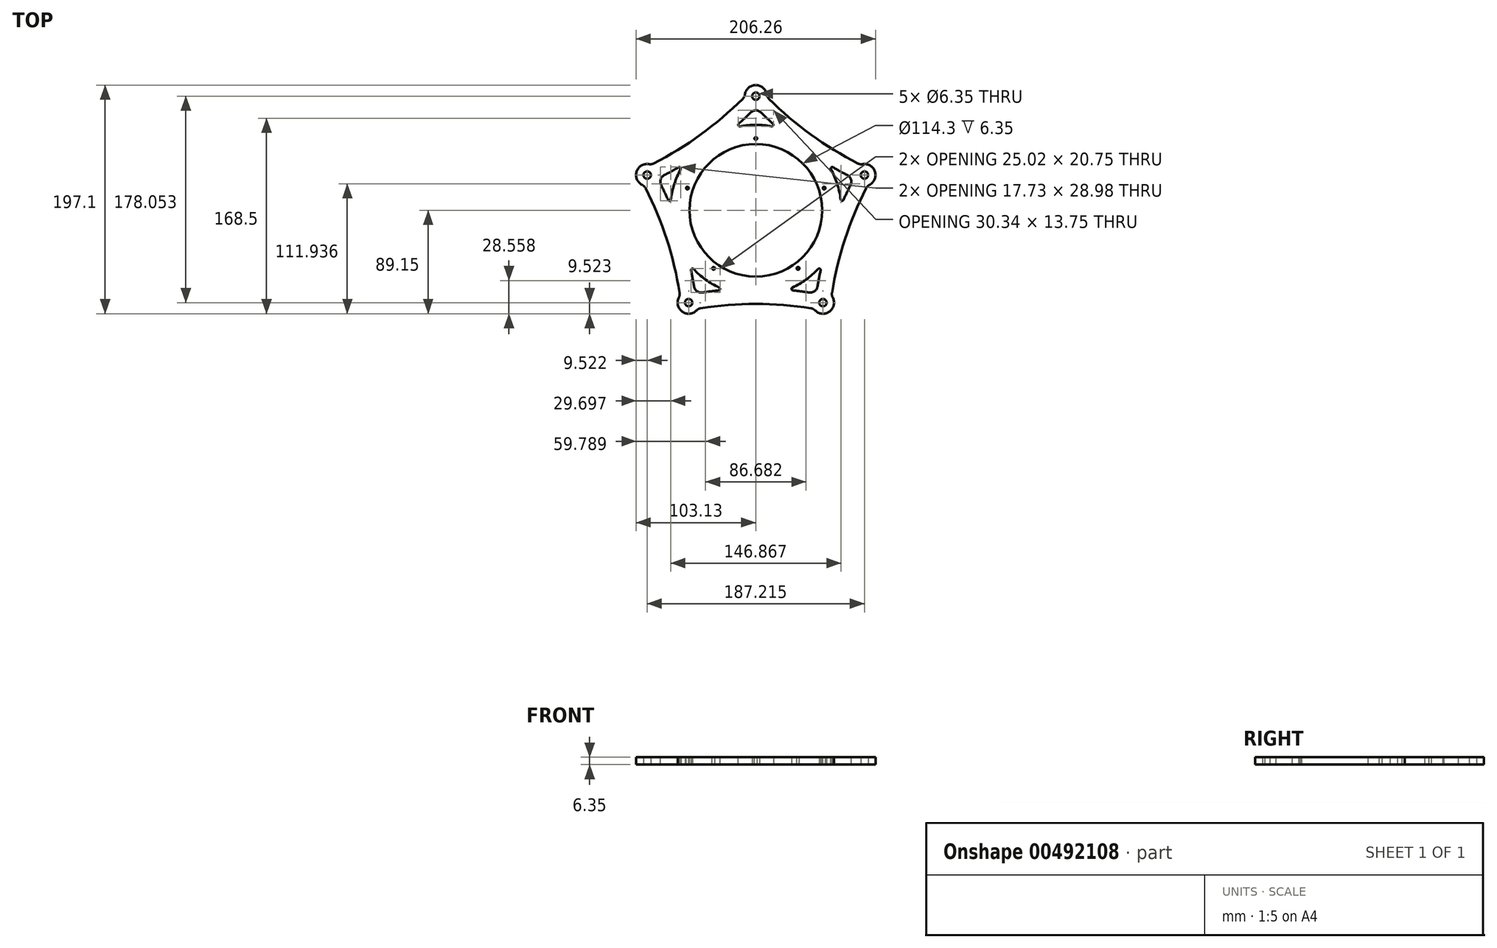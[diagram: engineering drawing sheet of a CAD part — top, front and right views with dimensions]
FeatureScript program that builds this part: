
annotation { "Feature Type Name" : "Feature", "Feature Type Description" : "" }
export const myFeature = defineFeature(function(context is Context, id is Id, definition is map)
    precondition{}
    {
        {
            var Q0;
            Q0=qCreatedBy(makeId("Top.planeOp"),FACE);
            var sketch = newSketch(context, id + "F0", { "sketchPlane" : qUnion([Q0])});
            skCircle(sketch, "E0", {"center": v(0, 0) * mm, "radius": 98.43 * mm, "construction": true});
            skCircle(sketch, "E1", {"center": v(0, 98.43) * mm, "radius": 3.18 * mm});
            skCircle(sketch, "E2.1.0", {"center": v(-93.6, 30.41) * mm, "radius": 3.18 * mm});
            skCircle(sketch, "E2.2.0", {"center": v(-57.85, -79.63) * mm, "radius": 3.18 * mm});
            skCircle(sketch, "E2.3.0", {"center": v(57.85, -79.63) * mm, "radius": 3.18 * mm});
            skCircle(sketch, "E2.4.0", {"center": v(93.6, 30.41) * mm, "radius": 3.18 * mm});
            skCircle(sketch, "E3", {"center": v(0, 98.43) * mm, "radius": 9.53 * mm, "construction": true});
            skCircle(sketch, "E4.1.0", {"center": v(-93.6, 30.41) * mm, "radius": 9.53 * mm, "construction": true});
            skCircle(sketch, "E4.2.0", {"center": v(-57.85, -79.63) * mm, "radius": 9.53 * mm, "construction": true});
            skCircle(sketch, "E4.3.0", {"center": v(57.85, -79.63) * mm, "radius": 9.53 * mm, "construction": true});
            skCircle(sketch, "E4.4.0", {"center": v(93.6, 30.41) * mm, "radius": 9.53 * mm, "construction": true});
            skArc(sketch, "E5", {"start": v(-90.23, 39.32) * mm, "mid": v(-47.46, 65.32) * mm, "end": v(-9.51, 97.96) * mm});
            skArc(sketch, "E6", {"start": v(9.51, 97.96) * mm, "mid": v(47.46, 65.32) * mm, "end": v(90.23, 39.32) * mm});
            skArc(sketch, "E7", {"start": v(96.1, 21.22) * mm, "mid": v(76.79, -24.95) * mm, "end": v(65.28, -73.66) * mm});
            skArc(sketch, "E8", {"start": v(49.89, -84.85) * mm, "mid": v(0, -80.74) * mm, "end": v(-49.89, -84.85) * mm});
            skArc(sketch, "E9", {"start": v(-65.28, -73.66) * mm, "mid": v(-76.79, -24.95) * mm, "end": v(-96.1, 21.22) * mm});
            skLineSegment(sketch, "E10", {"start": v(0, 0) * mm, "end": v(-93.6, 30.41) * mm, "construction": true});
            skLineSegment(sketch, "E11", {"start": v(0, 0) * mm, "end": v(93.6, 30.41) * mm, "construction": true});
            skLineSegment(sketch, "E12", {"start": v(0, 0) * mm, "end": v(57.85, -79.63) * mm, "construction": true});
            skLineSegment(sketch, "E13", {"start": v(0, 0) * mm, "end": v(-57.85, -79.63) * mm, "construction": true});
            skLineSegment(sketch, "E14", {"start": v(0, 0) * mm, "end": v(0, 98.43) * mm, "construction": true});
            skArc(sketch, "E15", {"start": v(-84.55, 27.47) * mm, "mid": v(-39.62, 54.54) * mm, "end": v(0, 88.9) * mm});
            skArc(sketch, "E16", {"start": v(0, 88.9) * mm, "mid": v(39.62, 54.54) * mm, "end": v(84.55, 27.47) * mm});
            skArc(sketch, "E17", {"start": v(84.55, 27.47) * mm, "mid": v(64.1, -20.83) * mm, "end": v(52.25, -71.92) * mm});
            skArc(sketch, "E18", {"start": v(52.25, -71.92) * mm, "mid": v(0, -67.4) * mm, "end": v(-52.25, -71.92) * mm});
            skArc(sketch, "E19", {"start": v(-52.25, -71.92) * mm, "mid": v(-64.1, -20.83) * mm, "end": v(-84.55, 27.47) * mm});
            skArc(sketch, "E20", {"start": v(-96.1, 21.22) * mm, "mid": v(-102.67, 33.36) * mm, "end": v(-90.23, 39.32) * mm});
            skArc(sketch, "E21", {"start": v(-9.51, 97.96) * mm, "mid": v(0, 107.95) * mm, "end": v(9.51, 97.96) * mm});
            skArc(sketch, "E22", {"start": v(90.23, 39.32) * mm, "mid": v(102.67, 33.36) * mm, "end": v(96.1, 21.22) * mm});
            skArc(sketch, "E23", {"start": v(65.28, -73.66) * mm, "mid": v(63.45, -87.33) * mm, "end": v(49.89, -84.85) * mm});
            skArc(sketch, "E24", {"start": v(-65.28, -73.66) * mm, "mid": v(-63.45, -87.33) * mm, "end": v(-49.89, -84.85) * mm});
            skSolve(sketch);
        }
        {
            var Q0;
            Q0 = qSketchRegion(id + "F0", true);
            extrude(context, id + "F1", {"entities" : qUnion([Q0]), "depth" : 6.35 * mm});
        }
        {
            var Q0;
            Q0=makeQuery(id+"F1.opExtrude","SWEPT_EDGE",EDGE,{"disambiguationData":[OSD([sQuery(id+"F0.wireOp",EDGE,"E15"),sQuery(id+"F0.wireOp",EDGE,"E16")])]});
            var Q1;
            Q1=makeQuery(id+"F1.opExtrude","SWEPT_EDGE",EDGE,{"disambiguationData":[OSD([sQuery(id+"F0.wireOp",EDGE,"E5"),sQuery(id+"F0.wireOp",EDGE,"E21")])]});
            var Q2;
            Q2=makeQuery(id+"F1.opExtrude","SWEPT_EDGE",EDGE,{"disambiguationData":[OSD([sQuery(id+"F0.wireOp",EDGE,"E6"),sQuery(id+"F0.wireOp",EDGE,"E21")])]});
            var Q3;
            Q3=makeQuery(id+"F1.opExtrude","SWEPT_EDGE",EDGE,{"disambiguationData":[OSD([sQuery(id+"F0.wireOp",EDGE,"E16"),sQuery(id+"F0.wireOp",EDGE,"E17")])]});
            var Q4;
            Q4=makeQuery(id+"F1.opExtrude","SWEPT_EDGE",EDGE,{"disambiguationData":[OSD([sQuery(id+"F0.wireOp",EDGE,"E7"),sQuery(id+"F0.wireOp",EDGE,"E22")])]});
            var Q5;
            Q5=makeQuery(id+"F1.opExtrude","SWEPT_EDGE",EDGE,{"disambiguationData":[OSD([sQuery(id+"F0.wireOp",EDGE,"E6"),sQuery(id+"F0.wireOp",EDGE,"E22")])]});
            var Q6;
            Q6=makeQuery(id+"F1.opExtrude","SWEPT_EDGE",EDGE,{"disambiguationData":[OSD([sQuery(id+"F0.wireOp",EDGE,"E7"),sQuery(id+"F0.wireOp",EDGE,"E23")])]});
            var Q7;
            Q7=makeQuery(id+"F1.opExtrude","SWEPT_EDGE",EDGE,{"disambiguationData":[OSD([sQuery(id+"F0.wireOp",EDGE,"E8"),sQuery(id+"F0.wireOp",EDGE,"E23")])]});
            var Q8;
            Q8=makeQuery(id+"F1.opExtrude","SWEPT_EDGE",EDGE,{"disambiguationData":[OSD([sQuery(id+"F0.wireOp",EDGE,"E17"),sQuery(id+"F0.wireOp",EDGE,"E18")])]});
            var Q9;
            Q9=makeQuery(id+"F1.opExtrude","SWEPT_EDGE",EDGE,{"disambiguationData":[OSD([sQuery(id+"F0.wireOp",EDGE,"E8"),sQuery(id+"F0.wireOp",EDGE,"E24")])]});
            var Q10;
            Q10=makeQuery(id+"F1.opExtrude","SWEPT_EDGE",EDGE,{"disambiguationData":[OSD([sQuery(id+"F0.wireOp",EDGE,"E9"),sQuery(id+"F0.wireOp",EDGE,"E24")])]});
            var Q11;
            Q11=makeQuery(id+"F1.opExtrude","SWEPT_EDGE",EDGE,{"disambiguationData":[OSD([sQuery(id+"F0.wireOp",EDGE,"E18"),sQuery(id+"F0.wireOp",EDGE,"E19")])]});
            var Q12;
            Q12=makeQuery(id+"F1.opExtrude","SWEPT_EDGE",EDGE,{"disambiguationData":[OSD([sQuery(id+"F0.wireOp",EDGE,"E15"),sQuery(id+"F0.wireOp",EDGE,"E19")])]});
            var Q13;
            Q13=makeQuery(id+"F1.opExtrude","SWEPT_EDGE",EDGE,{"disambiguationData":[OSD([sQuery(id+"F0.wireOp",EDGE,"E5"),sQuery(id+"F0.wireOp",EDGE,"E20")])]});
            var Q14;
            Q14=makeQuery(id+"F1.opExtrude","SWEPT_EDGE",EDGE,{"disambiguationData":[OSD([sQuery(id+"F0.wireOp",EDGE,"E9"),sQuery(id+"F0.wireOp",EDGE,"E20")])]});
            fillet(context, id + "F2", {"entities" : qUnion([Q0, Q1, Q2, Q3, Q4, Q5, Q6, Q7, Q8, Q9, Q10, Q11, Q12, Q13, Q14]), "radius" : 6.35 * mm, "tangentPropagation" : true, "allowEdgeOverflow" : false});
        }
        {
            var Q0;
            Q0=makeQuery(id+"F1.opExtrude","CAP_FACE",FACE,{"disambiguationData":[OSD([sQuery(id+"F0.wireOp",EDGE,"E1"),sQuery(id+"F0.wireOp",EDGE,"E2.1.0"),sQuery(id+"F0.wireOp",EDGE,"E2.2.0"),sQuery(id+"F0.wireOp",EDGE,"E2.3.0"),sQuery(id+"F0.wireOp",EDGE,"E2.4.0"),sQuery(id+"F0.wireOp",EDGE,"E5"),sQuery(id+"F0.wireOp",EDGE,"E6"),sQuery(id+"F0.wireOp",EDGE,"E7"),sQuery(id+"F0.wireOp",EDGE,"E8"),sQuery(id+"F0.wireOp",EDGE,"E9"),sQuery(id+"F0.wireOp",EDGE,"E15"),sQuery(id+"F0.wireOp",EDGE,"E16"),sQuery(id+"F0.wireOp",EDGE,"E17"),sQuery(id+"F0.wireOp",EDGE,"E18"),sQuery(id+"F0.wireOp",EDGE,"E19"),sQuery(id+"F0.wireOp",EDGE,"E20"),sQuery(id+"F0.wireOp",EDGE,"E21"),sQuery(id+"F0.wireOp",EDGE,"E22"),sQuery(id+"F0.wireOp",EDGE,"E23"),sQuery(id+"F0.wireOp",EDGE,"E24")])],"isStart":false});
            var sketch = newSketch(context, id + "F3", { "sketchPlane" : qUnion([Q0])});
            skCircle(sketch, "E25", {"center": v(0, 0) * mm, "radius": 66.68 * mm, "construction": true});
            skCircle(sketch, "E26", {"center": v(0, 0) * mm, "radius": 57.15 * mm});
            skCircle(sketch, "E27", {"center": v(0, 0) * mm, "radius": 73.76 * mm});
            skLineSegment(sketch, "E28", {"start": v(0, 57.15) * mm, "end": v(0, 66.68) * mm, "construction": true});
            skCircle(sketch, "E29", {"center": v(0, 61.91) * mm, "radius": 1.2 * mm});
            skCircle(sketch, "E30.1.0", {"center": v(-58.88, 19.13) * mm, "radius": 1.2 * mm});
            skCircle(sketch, "E30.2.0", {"center": v(-36.4, -50.09) * mm, "radius": 1.2 * mm});
            skCircle(sketch, "E30.3.0", {"center": v(36.4, -50.09) * mm, "radius": 1.2 * mm});
            skCircle(sketch, "E30.4.0", {"center": v(58.88, 19.13) * mm, "radius": 1.2 * mm});
            skSolve(sketch);
        }
        {
            var Q0;
            Q0 = qSketchRegion(id + "F3", true);
            var Q1;
            Q1=makeQuery(id+"F1.opExtrude","CAP_FACE",FACE,{"disambiguationData":[OSD([sQuery(id+"F0.wireOp",EDGE,"E1"),sQuery(id+"F0.wireOp",EDGE,"E2.1.0"),sQuery(id+"F0.wireOp",EDGE,"E2.2.0"),sQuery(id+"F0.wireOp",EDGE,"E2.3.0"),sQuery(id+"F0.wireOp",EDGE,"E2.4.0"),sQuery(id+"F0.wireOp",EDGE,"E5"),sQuery(id+"F0.wireOp",EDGE,"E6"),sQuery(id+"F0.wireOp",EDGE,"E7"),sQuery(id+"F0.wireOp",EDGE,"E8"),sQuery(id+"F0.wireOp",EDGE,"E9"),sQuery(id+"F0.wireOp",EDGE,"E15"),sQuery(id+"F0.wireOp",EDGE,"E16"),sQuery(id+"F0.wireOp",EDGE,"E17"),sQuery(id+"F0.wireOp",EDGE,"E18"),sQuery(id+"F0.wireOp",EDGE,"E19"),sQuery(id+"F0.wireOp",EDGE,"E20"),sQuery(id+"F0.wireOp",EDGE,"E21"),sQuery(id+"F0.wireOp",EDGE,"E22"),sQuery(id+"F0.wireOp",EDGE,"E23"),sQuery(id+"F0.wireOp",EDGE,"E24")])],"isStart":true});
            extrude(context, id + "F4", {"entities" : qUnion([Q0]), "operationType" : NewBodyOperationType.ADD, "endBound" : BoundingType.UP_TO_SURFACE, "oppositeDirection" : true, "endBoundEntityFace" : qUnion([Q1]), "depth" : 25.4 * mm});
        }
        {
            var Q0;
            Q0=makeQuery(id+"F4.boolean.opBoolean","INTERSECT",EDGE,{"disambiguationData":[OD(1.0)],"derivedFrom":[makeQuery(id+"F1.opExtrude","SWEPT_FACE",FACE,{"disambiguationData":[OSD([sQuery(id+"F0.wireOp",EDGE,"E19")])]}),makeQuery(id+"F4.opExtrude","SWEPT_FACE",FACE,{"disambiguationData":[OSD([sQuery(id+"F3.wireOp",EDGE,"E27")])]})]});
            var Q1;
            Q1=makeQuery(id+"F4.boolean.opBoolean","INTERSECT",EDGE,{"disambiguationData":[OD(1.0)],"derivedFrom":[makeQuery(id+"F1.opExtrude","SWEPT_FACE",FACE,{"disambiguationData":[OSD([sQuery(id+"F0.wireOp",EDGE,"E18")])]}),makeQuery(id+"F4.opExtrude","SWEPT_FACE",FACE,{"disambiguationData":[OSD([sQuery(id+"F3.wireOp",EDGE,"E27")])]})]});
            var Q2;
            Q2=makeQuery(id+"F4.boolean.opBoolean","INTERSECT",EDGE,{"disambiguationData":[OD(1.0)],"derivedFrom":[makeQuery(id+"F1.opExtrude","SWEPT_FACE",FACE,{"disambiguationData":[OSD([sQuery(id+"F0.wireOp",EDGE,"E17")])]}),makeQuery(id+"F4.opExtrude","SWEPT_FACE",FACE,{"disambiguationData":[OSD([sQuery(id+"F3.wireOp",EDGE,"E27")])]})]});
            var Q3;
            Q3=makeQuery(id+"F4.boolean.opBoolean","INTERSECT",EDGE,{"disambiguationData":[OD(0.0)],"derivedFrom":[makeQuery(id+"F1.opExtrude","SWEPT_FACE",FACE,{"disambiguationData":[OSD([sQuery(id+"F0.wireOp",EDGE,"E18")])]}),makeQuery(id+"F4.opExtrude","SWEPT_FACE",FACE,{"disambiguationData":[OSD([sQuery(id+"F3.wireOp",EDGE,"E27")])]})]});
            var Q4;
            Q4=makeQuery(id+"F4.boolean.opBoolean","INTERSECT",EDGE,{"disambiguationData":[OD(1.0)],"derivedFrom":[makeQuery(id+"F1.opExtrude","SWEPT_FACE",FACE,{"disambiguationData":[OSD([sQuery(id+"F0.wireOp",EDGE,"E16")])]}),makeQuery(id+"F4.opExtrude","SWEPT_FACE",FACE,{"disambiguationData":[OSD([sQuery(id+"F3.wireOp",EDGE,"E27")])]})]});
            var Q5;
            Q5=makeQuery(id+"F4.boolean.opBoolean","INTERSECT",EDGE,{"disambiguationData":[OD(0.0)],"derivedFrom":[makeQuery(id+"F1.opExtrude","SWEPT_FACE",FACE,{"disambiguationData":[OSD([sQuery(id+"F0.wireOp",EDGE,"E17")])]}),makeQuery(id+"F4.opExtrude","SWEPT_FACE",FACE,{"disambiguationData":[OSD([sQuery(id+"F3.wireOp",EDGE,"E27")])]})]});
            var Q6;
            Q6=makeQuery(id+"F4.boolean.opBoolean","INTERSECT",EDGE,{"disambiguationData":[OD(1.0)],"derivedFrom":[makeQuery(id+"F1.opExtrude","SWEPT_FACE",FACE,{"disambiguationData":[OSD([sQuery(id+"F0.wireOp",EDGE,"E15")])]}),makeQuery(id+"F4.opExtrude","SWEPT_FACE",FACE,{"disambiguationData":[OSD([sQuery(id+"F3.wireOp",EDGE,"E27")])]})]});
            var Q7;
            Q7=makeQuery(id+"F4.boolean.opBoolean","INTERSECT",EDGE,{"disambiguationData":[OD(0.0)],"derivedFrom":[makeQuery(id+"F1.opExtrude","SWEPT_FACE",FACE,{"disambiguationData":[OSD([sQuery(id+"F0.wireOp",EDGE,"E16")])]}),makeQuery(id+"F4.opExtrude","SWEPT_FACE",FACE,{"disambiguationData":[OSD([sQuery(id+"F3.wireOp",EDGE,"E27")])]})]});
            var Q8;
            Q8=makeQuery(id+"F4.boolean.opBoolean","INTERSECT",EDGE,{"disambiguationData":[OD(0.0)],"derivedFrom":[makeQuery(id+"F1.opExtrude","SWEPT_FACE",FACE,{"disambiguationData":[OSD([sQuery(id+"F0.wireOp",EDGE,"E19")])]}),makeQuery(id+"F4.opExtrude","SWEPT_FACE",FACE,{"disambiguationData":[OSD([sQuery(id+"F3.wireOp",EDGE,"E27")])]})]});
            var Q9;
            Q9=makeQuery(id+"F4.boolean.opBoolean","INTERSECT",EDGE,{"disambiguationData":[OD(0.0)],"derivedFrom":[makeQuery(id+"F1.opExtrude","SWEPT_FACE",FACE,{"disambiguationData":[OSD([sQuery(id+"F0.wireOp",EDGE,"E15")])]}),makeQuery(id+"F4.opExtrude","SWEPT_FACE",FACE,{"disambiguationData":[OSD([sQuery(id+"F3.wireOp",EDGE,"E27")])]})]});
            fillet(context, id + "F5", {"entities" : qUnion([Q0, Q1, Q2, Q3, Q4, Q5, Q6, Q7, Q8, Q9]), "radius" : 1.27 * mm, "tangentPropagation" : true, "allowEdgeOverflow" : false});
        }
    });
